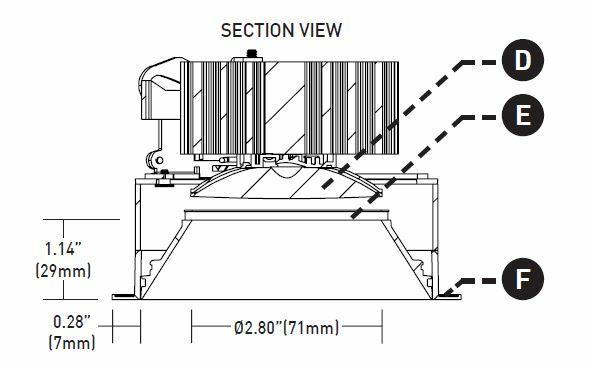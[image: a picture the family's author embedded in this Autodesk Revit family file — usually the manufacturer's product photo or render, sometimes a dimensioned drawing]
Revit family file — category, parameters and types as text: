
# Revit family: Lighting-Recessed-Lucifer-Fraxion 3 Trimless Round
name_source: partatom
category: Lighting Fixtures
revit_build: Autodesk Revit 2016 (Build: 20170117_1200(x64)
units: mm (PartAtom-declared; Revit-internal decimal feet)

## family parameters
Cut with Voids When Loaded = No
Host = Face
Light Source = Yes
Part Type = Normal
Room Calculation Point = No
Round Connector Dimension = Use Diameter
Shared = No

## types (3) — shared parameters
Apparent Load = 0 VA
Color Filter = 16777215
Default Elevation = 48 "
Description = Recessed LED Downlight Remodel
Dimming Lamp Color Temperature Shift = <None>
Emit Shape Visible in Rendering = No
Emit from Circle Diameter = 3 "
Lamp = LED
Manufacturer = Lucifer Lighting
Number of Poles = 1
Photometric Web File = Load File
Power Factor = 1
Tilt Angle = -90.00°
URL = https://www.luciferlighting.com
Voltage = 0 V

## per-type parameters (varying)
| type | Height | Length | Width |
| F3RTFS | 6.7 " | 9.74 " | 9.83 " |
| F3RTAS | 6.7 " | 9.74 " | 9.83 " |
| F3RTWW | 2.1 " | 13 " | 7.5 " |

note: column(s) folded — value = type name in every type: Model

## geometry (parser evidence)
native form markers: Sweep x3
no freeform markers — native parametric forms only
